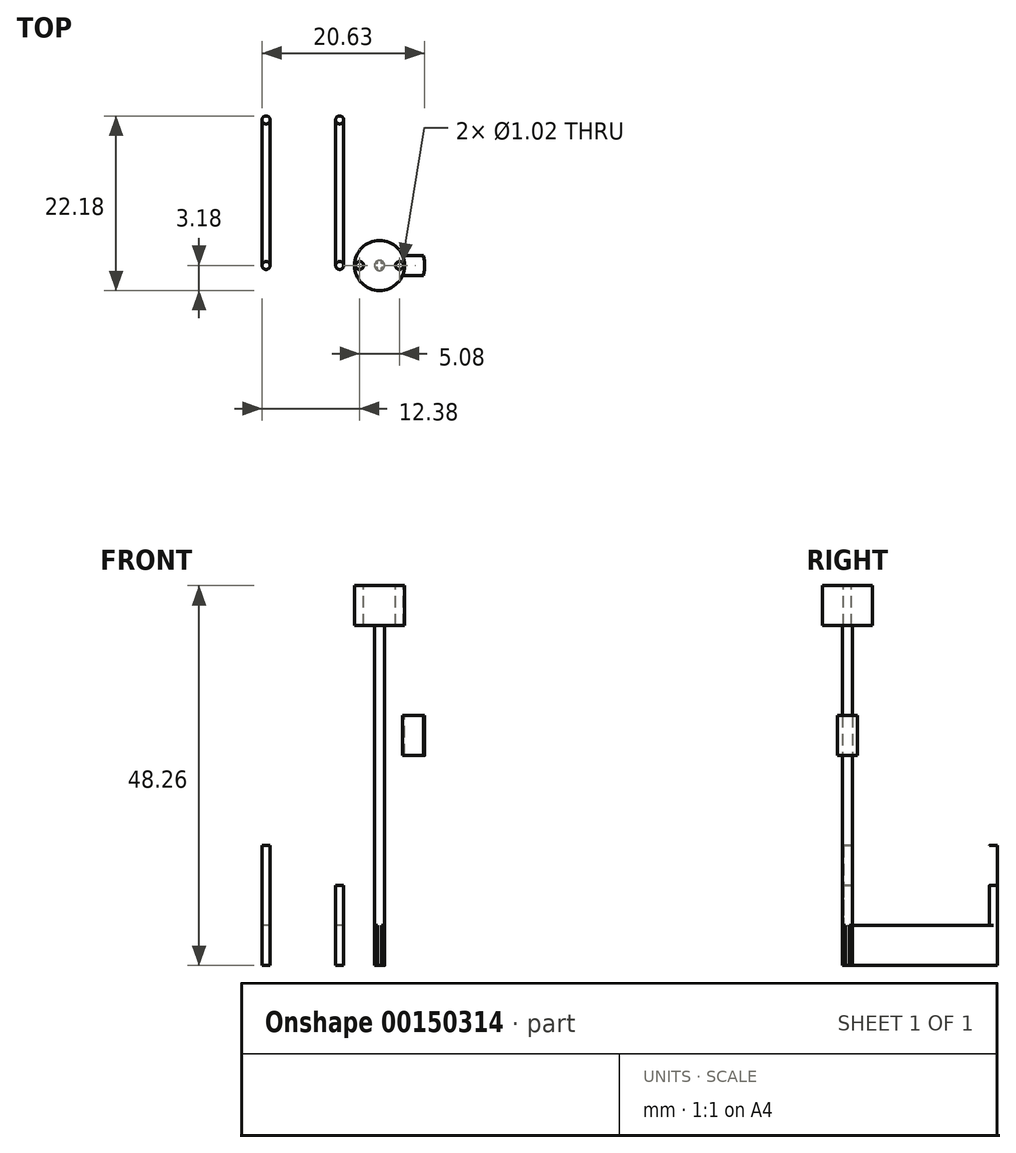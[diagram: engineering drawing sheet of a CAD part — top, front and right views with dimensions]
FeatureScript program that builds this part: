
annotation { "Feature Type Name" : "Feature", "Feature Type Description" : "" }
export const myFeature = defineFeature(function(context is Context, id is Id, definition is map)
    precondition{}
    {
        {
            var Q0;
            Q0=qCreatedBy(makeId("Top.planeOp"),FACE);
            var sketch = newSketch(context, id + "F0", { "sketchPlane" : qUnion([Q0])});
            skCircle(sketch, "E0", {"center": v(0, 0) * mm, "radius": 0.64 * mm});
            skSolve(sketch);
        }
        {
            var Q0;
            Q0=makeQuery(id+"F0.imprint","IMPRINT",FACE,{"disambiguationData":[TD([[makeQuery(id+"F0.imprint","IMPRINT",EDGE,{"derivedFrom":sQuery(id+"F0.wireOp",EDGE,"E0")}),1.0]])]});
            extrude(context, id + "F1", {"entities" : qUnion([Q0]), "depth" : 48.26 * mm});
        }
        {
            var Q0;
            Q0=makeQuery(id+"F1.opExtrude","CAP_FACE",FACE,{"disambiguationData":[OSD([sQuery(id+"F0.wireOp",EDGE,"E0")])],"isStart":false});
            var sketch = newSketch(context, id + "F2", { "sketchPlane" : qUnion([Q0])});
            skCircle(sketch, "E1", {"center": v(0, 0) * mm, "radius": 3.18 * mm});
            skLineSegment(sketch, "E2", {"start": v(0, 0) * mm, "end": v(3.18, 0) * mm});
            skLineSegment(sketch, "E3", {"start": v(3.18, 0) * mm, "end": v(-3.18, 0) * mm});
            skLineSegment(sketch, "E4", {"start": v(-3.18, 0) * mm, "end": v(-2.54, 0) * mm});
            skCircle(sketch, "E5", {"center": v(-2.54, 0) * mm, "radius": 0.5 * mm});
            skLineSegment(sketch, "E6", {"start": v(0, 0) * mm, "end": v(0, 3.18) * mm});
            skCircle(sketch, "E7.MirrorC", {"center": v(2.54, 0) * mm, "radius": 0.5 * mm});
            skSolve(sketch);
        }
        {
            var Q0;
            Q0 = qSketchRegion(id + "F2", true);
            extrude(context, id + "F3", {"entities" : qUnion([Q0]), "operationType" : NewBodyOperationType.ADD, "oppositeDirection" : true, "depth" : 5.08 * mm});
        }
        {
            var Q0;
            Q0=qCreatedBy(makeId("Top.planeOp"),FACE);
            var sketch = newSketch(context, id + "F4", { "sketchPlane" : qUnion([Q0])});
            skLineSegment(sketch, "E8", {"start": v(0, 0) * mm, "end": v(-4.57, 0) * mm});
            skLineSegment(sketch, "E9.bottom", {"start": v(-4.57, 0) * mm, "end": v(-5.58, 0) * mm});
            skLineSegment(sketch, "E9.top", {"start": v(-4.57, 18.5) * mm, "end": v(-5.58, 18.5) * mm});
            skLineSegment(sketch, "E9.left", {"start": v(-4.57, 0) * mm, "end": v(-4.57, 18.5) * mm});
            skLineSegment(sketch, "E9.right", {"start": v(-5.58, 0) * mm, "end": v(-5.58, 18.5) * mm});
            skCircle(sketch, "E10", {"center": v(-5.07, 0) * mm, "radius": 0.5 * mm});
            skCircle(sketch, "E11", {"center": v(-5.07, 18.5) * mm, "radius": 0.5 * mm});
            skLineSegment(sketch, "E12", {"start": v(0, 0) * mm, "end": v(-14.41, 0) * mm});
            skCircle(sketch, "E13", {"center": v(-14.41, 0) * mm, "radius": 0.5 * mm});
            skLineSegment(sketch, "E14.bottom", {"start": v(-13.9, 0) * mm, "end": v(-14.92, 0) * mm});
            skLineSegment(sketch, "E14.top", {"start": v(-13.9, 18.5) * mm, "end": v(-14.92, 18.5) * mm});
            skLineSegment(sketch, "E14.left", {"start": v(-13.9, 0) * mm, "end": v(-13.9, 18.5) * mm});
            skLineSegment(sketch, "E14.right", {"start": v(-14.92, 0) * mm, "end": v(-14.92, 18.5) * mm});
            skCircle(sketch, "E15", {"center": v(-14.41, 18.5) * mm, "radius": 0.5 * mm});
            skSolve(sketch);
        }
        {
            var Q0;
            Q0 = qSketchRegion(id + "F4", true);
            extrude(context, id + "F5", {"entities" : qUnion([Q0]), "depth" : 5.08 * mm});
        }
        {
            var Q0;
            Q0=makeQuery(id+"F5.opExtrude","CAP_FACE",FACE,{"disambiguationData":[OSD([sQuery(id+"F4.wireOp",EDGE,"E9.left"),sQuery(id+"F4.wireOp",EDGE,"E9.right"),sQuery(id+"F4.wireOp",EDGE,"E10"),sQuery(id+"F4.wireOp",EDGE,"E11")])],"isStart":false});
            var sketch = newSketch(context, id + "F6", { "sketchPlane" : qUnion([Q0])});
            skCircle(sketch, "E16", {"center": v(-5.07, 18.5) * mm, "radius": 0.5 * mm});
            skCircle(sketch, "E17", {"center": v(-5.07, 0) * mm, "radius": 0.5 * mm});
            skSolve(sketch);
        }
        {
            var Q0;
            Q0 = qSketchRegion(id + "F6", true);
            extrude(context, id + "F7", {"entities" : qUnion([Q0]), "operationType" : NewBodyOperationType.ADD, "depth" : 5.08 * mm});
        }
        {
            var Q0;
            Q0=makeQuery(id+"F5.opExtrude","CAP_FACE",FACE,{"disambiguationData":[OSD([sQuery(id+"F4.wireOp",EDGE,"E13"),sQuery(id+"F4.wireOp",EDGE,"E14.left"),sQuery(id+"F4.wireOp",EDGE,"E14.right"),sQuery(id+"F4.wireOp",EDGE,"E15")])],"isStart":false});
            var sketch = newSketch(context, id + "F8", { "sketchPlane" : qUnion([Q0])});
            skCircle(sketch, "E18", {"center": v(-14.41, 18.5) * mm, "radius": 0.5 * mm});
            skCircle(sketch, "E19", {"center": v(-14.41, 0) * mm, "radius": 0.5 * mm});
            skSolve(sketch);
        }
        {
            var Q0;
            Q0 = qSketchRegion(id + "F8", true);
            extrude(context, id + "F9", {"entities" : qUnion([Q0]), "operationType" : NewBodyOperationType.ADD, "depth" : 10.16 * mm});
        }
        {
            var Q0;
            Q0=qCreatedBy(makeId("Top.planeOp"),FACE);
            cPlane(context, id + "F10", {"entities" : qUnion([Q0]), "cplaneType" : CPlaneType.OFFSET, "offset" : 31.75 * mm, "width" : 152.4 * mm, "height" : 152.4 * mm});
        }
        {
            var Q0;
            Q0=qCreatedBy(id+"F10.planeOp",FACE);
            var sketch = newSketch(context, id + "F11", { "sketchPlane" : qUnion([Q0])});
            skLineSegment(sketch, "E20", {"start": v(0, 0) * mm, "end": v(3.18, 0) * mm});
            skLineSegment(sketch, "E21.bottom", {"start": v(5.57, 1.27) * mm, "end": v(0.78, 1.27) * mm});
            skLineSegment(sketch, "E21.top", {"start": v(5.57, -1.27) * mm, "end": v(0.78, -1.27) * mm});
            skLineSegment(sketch, "E21.left", {"start": v(5.57, 1.27) * mm, "end": v(5.57, -1.27) * mm});
            skLineSegment(sketch, "E21.right", {"start": v(0.78, 1.27) * mm, "end": v(0.78, -1.27) * mm});
            skPoint(sketch, "E21.middle", {"position": v(3.18, 0) * mm});
            skCircle(sketch, "E22", {"center": v(0, 0) * mm, "radius": 3.18 * mm});
            skCircle(sketch, "E23", {"center": v(0, 0) * mm, "radius": 5.72 * mm});
            skSolve(sketch);
        }
        {
            var Q0;
            {var subQ4=sQuery(id+"F11.wireOp",EDGE,"E21.left");Q0=makeQuery(id+"F11.imprint","IMPRINT",FACE,{"disambiguationData":[TD([[makeQuery(id+"F11.imprint","IMPRINT",EDGE,{"derivedFrom":subQ4}),-1.0]])]});}
            var Q1;
            {var subQ0=sQuery(id+"F11.wireOp",EDGE,"E21.left");Q1=makeQuery(id+"F11.imprint","IMPRINT",FACE,{"disambiguationData":[TD([[makeQuery(id+"F11.imprint","IMPRINT",EDGE,{"derivedFrom":subQ0}),1.0]])]});}
            extrude(context, id + "F12", {"entities" : qUnion([Q0, Q1]), "operationType" : NewBodyOperationType.ADD, "oppositeDirection" : true, "depth" : 5.08 * mm});
        }
        {
            var Q0;
            Q0=makeQuery(id+"F1.opExtrude","CAP_FACE",FACE,{"disambiguationData":[OSD([sQuery(id+"F0.wireOp",EDGE,"E0")])],"isStart":true});
            var sketch = newSketch(context, id + "F13", { "sketchPlane" : qUnion([Q0])});
            skCircle(sketch, "E24", {"center": v(0, 0) * mm, "radius": 0.64 * mm});
            skLineSegment(sketch, "E25.bottom", {"start": v(6.88, 0.25) * mm, "end": v(-6.88, 0.25) * mm});
            skLineSegment(sketch, "E25.top", {"start": v(6.88, -0.25) * mm, "end": v(-6.88, -0.25) * mm});
            skLineSegment(sketch, "E25.left", {"start": v(6.88, 0.25) * mm, "end": v(6.88, -0.25) * mm});
            skLineSegment(sketch, "E25.right", {"start": v(-6.88, 0.25) * mm, "end": v(-6.88, -0.25) * mm});
            skLineSegment(sketch, "E26.bottom", {"start": v(0.25, 4.89) * mm, "end": v(-0.25, 4.89) * mm});
            skLineSegment(sketch, "E26.top", {"start": v(0.25, -4.89) * mm, "end": v(-0.25, -4.89) * mm});
            skLineSegment(sketch, "E26.left", {"start": v(0.25, 4.89) * mm, "end": v(0.25, -4.89) * mm});
            skLineSegment(sketch, "E26.right", {"start": v(-0.25, 4.89) * mm, "end": v(-0.25, -4.89) * mm});
            skSolve(sketch);
        }
        {
            var Q0;
            {var subQ0=sQuery(id+"F13.wireOp",EDGE,"E26.left");var subQ1=sQuery(id+"F13.wireOp",EDGE,"E24");var subQ2=makeQuery(id+"F13.imprint","INTERSECT",VERTEX,{"disambiguationData":[OD(1.0)],"derivedFrom":[subQ1,subQ0]});Q0=makeQuery(id+"F13.imprint","IMPRINT",FACE,{"disambiguationData":[TD([[makeQuery(id+"F13.imprint","IMPRINT",EDGE,{"disambiguationData":[TD([[subQ2,-1.0]])],"derivedFrom":subQ1}),-1.0]])]});}
            var Q1;
            {var subQ0=sQuery(id+"F13.wireOp",EDGE,"E26.left");var subQ1=sQuery(id+"F13.wireOp",EDGE,"E24");var subQ2=makeQuery(id+"F13.imprint","INTERSECT",VERTEX,{"disambiguationData":[OD(0.0)],"derivedFrom":[subQ1,subQ0]});Q1=makeQuery(id+"F13.imprint","IMPRINT",FACE,{"disambiguationData":[TD([[makeQuery(id+"F13.imprint","IMPRINT",EDGE,{"disambiguationData":[TD([[subQ2,1.0]])],"derivedFrom":subQ1}),-1.0]])]});}
            var Q2;
            {var subQ0=sQuery(id+"F13.wireOp",EDGE,"E26.right");var subQ1=sQuery(id+"F13.wireOp",EDGE,"E24");var subQ2=makeQuery(id+"F13.imprint","INTERSECT",VERTEX,{"disambiguationData":[OD(0.0)],"derivedFrom":[subQ1,subQ0]});Q2=makeQuery(id+"F13.imprint","IMPRINT",FACE,{"disambiguationData":[TD([[makeQuery(id+"F13.imprint","IMPRINT",EDGE,{"disambiguationData":[TD([[subQ2,-1.0]])],"derivedFrom":subQ1}),-1.0]])]});}
            var Q3;
            {var subQ0=sQuery(id+"F13.wireOp",EDGE,"E25.bottom");var subQ1=sQuery(id+"F13.wireOp",EDGE,"E24");var subQ2=makeQuery(id+"F13.imprint","INTERSECT",VERTEX,{"disambiguationData":[OD(0.0)],"derivedFrom":[subQ1,subQ0]});Q3=makeQuery(id+"F13.imprint","IMPRINT",FACE,{"disambiguationData":[TD([[makeQuery(id+"F13.imprint","IMPRINT",EDGE,{"disambiguationData":[TD([[subQ2,-1.0]])],"derivedFrom":subQ1}),-1.0]])]});}
            extrude(context, id + "F14", {"entities" : qUnion([Q0, Q1, Q2, Q3]), "operationType" : NewBodyOperationType.REMOVE, "oppositeDirection" : true, "depth" : 5.08 * mm});
        }
    });
